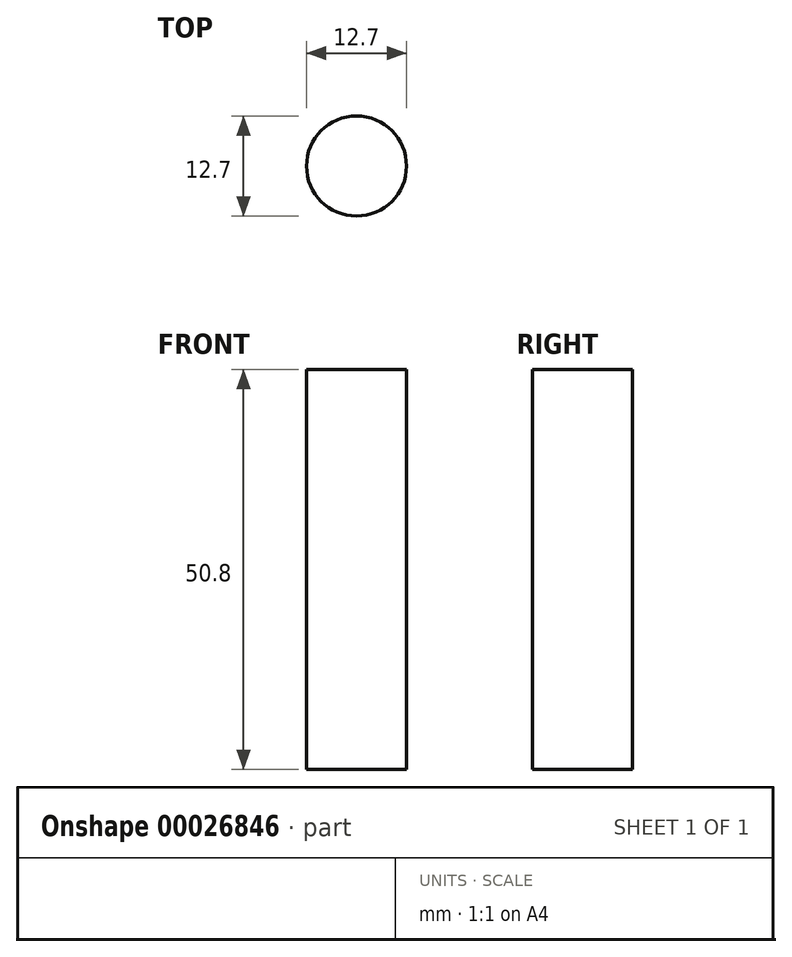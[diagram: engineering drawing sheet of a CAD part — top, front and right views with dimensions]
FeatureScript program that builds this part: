
annotation { "Feature Type Name" : "Feature", "Feature Type Description" : "" }
export const myFeature = defineFeature(function(context is Context, id is Id, definition is map)
    precondition{}
    {
        {
            var Q0;
            Q0=qCreatedBy(makeId("Front.planeOp"),FACE);
            var sketch = newSketch(context, id + "F0", { "sketchPlane" : qUnion([Q0])});
            skLineSegment(sketch, "E0.bottom", {"start": v(0, 14.66) * mm, "end": v(6.35, 14.66) * mm});
            skLineSegment(sketch, "E0.top", {"start": v(0, -36.14) * mm, "end": v(6.35, -36.14) * mm});
            skLineSegment(sketch, "E0.left", {"start": v(0, 14.66) * mm, "end": v(0, -36.14) * mm});
            skLineSegment(sketch, "E0.right", {"start": v(6.35, 14.66) * mm, "end": v(6.35, -36.14) * mm});
            skSolve(sketch);
        }
        {
            var Q0;
            Q0=makeQuery(id+"F0.imprint","IMPRINT",FACE,{"disambiguationData":[TD([[makeQuery(id+"F0.imprint","IMPRINT",EDGE,{"derivedFrom":sQuery(id+"F0.wireOp",EDGE,"E0.bottom")}),-1.0]])]});
            var Q1;
            Q1=sQuery(id+"F0.wireOp",EDGE,"E0.left");
            revolve(context, id + "F1", {"entities" : qUnion([Q0]), "axis" : qUnion([Q1]), "revolveType" : RevolveType.FULL});
        }
    });
